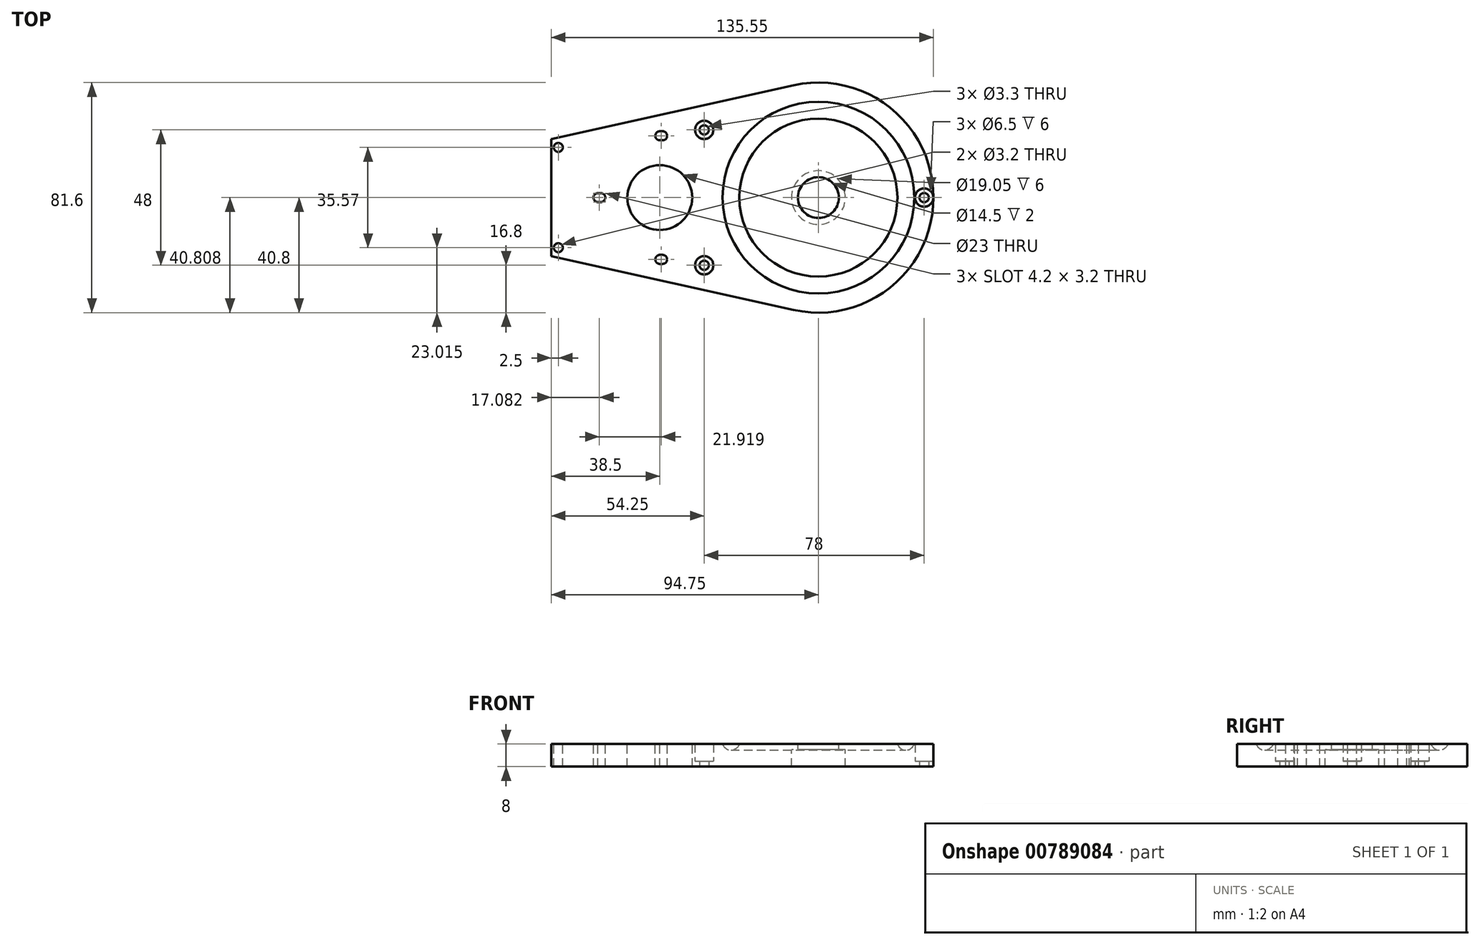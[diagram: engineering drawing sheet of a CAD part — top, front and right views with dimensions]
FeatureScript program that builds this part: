
annotation { "Feature Type Name" : "Feature", "Feature Type Description" : "" }
export const myFeature = defineFeature(function(context is Context, id is Id, definition is map)
    precondition{}
    {
        {
            var Q0;
            Q0=qCreatedBy(makeId("Top.planeOp"),FACE);
            var sketch = newSketch(context, id + "F0", { "sketchPlane" : qUnion([Q0])});
            skCircle(sketch, "E0", {"center": v(0, 0) * mm, "radius": 40.8 * mm});
            skSolve(sketch);
        }
        {
            var Q0;
            Q0=qSketchRegion(id+"F0",true);
            extrude(context, id + "F1", {"entities" : qUnion([Q0]), "depth" : 8 * mm, "offsetDistance" : 25 * mm});
        }
        {
            var Q0;
            Q0=qCreatedBy(makeId("Right.planeOp"),FACE);
            var sketch = newSketch(context, id + "F2", { "sketchPlane" : qUnion([Q0])});
            skLineSegment(sketch, "E1", {"start": v(0, 0) * mm, "end": v(0, 8) * mm});
            skLineSegment(sketch, "E2", {"start": v(0, 8) * mm, "end": v(7.25, 8) * mm});
            skLineSegment(sketch, "E3", {"start": v(7.25, 8) * mm, "end": v(7.25, 6) * mm});
            skLineSegment(sketch, "E4", {"start": v(7.25, 6) * mm, "end": v(9.53, 6) * mm});
            skLineSegment(sketch, "E5", {"start": v(9.53, 6) * mm, "end": v(9.53, 0) * mm});
            skLineSegment(sketch, "E6", {"start": v(9.53, 0) * mm, "end": v(0, 0) * mm});
            skLineSegment(sketch, "E7", {"start": v(0, 8) * mm, "end": v(0, 13.47) * mm, "construction": true});
            skSolve(sketch);
        }
        {
            var Q0;
            Q0=qSketchRegion(id+"F2",true);
            var Q1;
            Q1=sQuery(id+"F2.wireOp",EDGE,"E7");
            revolve(context, id + "F3", {"operationType" : NewBodyOperationType.REMOVE, "entities" : qUnion([Q0]), "axis" : qUnion([Q1]), "revolveType" : RevolveType.FULL, "oppositeDirection" : true});
        }
        {
            var Q0;
            Q0=qCreatedBy(makeId("Right.planeOp"),FACE);
            var sketch = newSketch(context, id + "F4", { "sketchPlane" : qUnion([Q0])});
            skCircle(sketch, "E8", {"center": v(31, 9) * mm, "radius": 3.15 * mm});
            skLineSegment(sketch, "E9", {"start": v(0, -0.8) * mm, "end": v(0, 13.57) * mm, "construction": true});
            skSolve(sketch);
        }
        {
            var Q0;
            Q0=qSketchRegion(id+"F4",true);
            var Q1;
            Q1=sQuery(id+"F4.wireOp",EDGE,"E9");
            revolve(context, id + "F5", {"operationType" : NewBodyOperationType.REMOVE, "entities" : qUnion([Q0]), "axis" : qUnion([Q1]), "revolveType" : RevolveType.FULL, "oppositeDirection" : true});
        }
        {
            var Q0;
            Q0=qCreatedBy(makeId("Top.planeOp"),FACE);
            var sketch = newSketch(context, id + "F6", { "sketchPlane" : qUnion([Q0])});
            skLineSegment(sketch, "E10.bottom", {"start": v(-36, 19.2) * mm, "end": v(-40.8, 19.2) * mm});
            skLineSegment(sketch, "E10.top", {"start": v(-36, -19.2) * mm, "end": v(-40.8, -19.2) * mm});
            skLineSegment(sketch, "E10.left", {"start": v(-36, 19.2) * mm, "end": v(-36, -19.2) * mm});
            skLineSegment(sketch, "E10.right", {"start": v(-40.8, 19.2) * mm, "end": v(-40.8, -19.2) * mm});
            skSolve(sketch);
        }
        {
            var Q0;
            Q0=qSketchRegion(id+"F6",true);
            extrude(context, id + "F7", {"entities" : qUnion([Q0]), "operationType" : NewBodyOperationType.REMOVE, "endBound" : BoundingType.THROUGH_ALL, "depth" : 25 * mm});
        }
        {
            var Q0;
            Q0=qCreatedBy(makeId("Top.planeOp"),FACE);
            var sketch = newSketch(context, id + "F8", { "sketchPlane" : qUnion([Q0])});
            skLineSegment(sketch, "E11", {"start": v(-94.75, -20.79) * mm, "end": v(-94.75, 20.79) * mm});
            skLineSegment(sketch, "E12", {"start": v(-94.75, 20.79) * mm, "end": v(-8.83, 39.83) * mm});
            skLineSegment(sketch, "E13", {"start": v(0, 0) * mm, "end": v(-51.86, 0) * mm, "construction": true});
            skArc(sketch, "E14.0", {"start": v(-8.83, 39.83) * mm, "mid": v(-24.68, 32.5) * mm, "end": v(-36, 19.2) * mm});
            skPoint(sketch, "E15.orphan", {"position": v(-36, -19.2) * mm});
            skLineSegment(sketch, "E16.MirrorCS", {"start": v(-94.75, -20.79) * mm, "end": v(-8.83, -39.83) * mm});
            skArc(sketch, "E17.MirrorCS", {"start": v(-8.83, -39.83) * mm, "mid": v(-24.68, -32.5) * mm, "end": v(-36, -19.2) * mm});
            skLineSegment(sketch, "E18", {"start": v(-36, 19.2) * mm, "end": v(-36, -19.2) * mm});
            skSolve(sketch);
        }
        {
            var Q0;
            Q0=qSketchRegion(id+"F8",true);
            var Q1;
            {var subQ0=sQuery(id+"F0.wireOp",EDGE,"E0");Q1=makeQuery(id+"F5.boolean.opBoolean","SPLIT",FACE,{"disambiguationData":[TD([makeQuery(id+"F1.opExtrude","SWEPT_FACE",FACE,{"disambiguationData":[OSD([subQ0])]})])],"derivedFrom":makeQuery(id+"F1.opExtrude","CAP_FACE",FACE,{"disambiguationData":[OSD([subQ0])],"isStart":false})});}
            extrude(context, id + "F9", {"entities" : qUnion([Q0]), "operationType" : NewBodyOperationType.ADD, "endBound" : BoundingType.UP_TO_SURFACE, "endBoundEntityFace" : qUnion([Q1]), "depth" : 25 * mm});
        }
        {
            var Q0;
            {var subQ0=sQuery(id+"F0.wireOp",EDGE,"E0");Q0=makeQuery(id+"F9.boolean.opBoolean","MERGE",FACE,{"derivedFrom":[makeQuery(id+"F5.boolean.opBoolean","SPLIT",FACE,{"disambiguationData":[TD([makeQuery(id+"F1.opExtrude","SWEPT_FACE",FACE,{"disambiguationData":[OSD([subQ0])]})])],"derivedFrom":makeQuery(id+"F1.opExtrude","CAP_FACE",FACE,{"disambiguationData":[OSD([subQ0])],"isStart":false})}),makeQuery(id+"F9.opExtrude","CAP_FACE",FACE,{"disambiguationData":[OSD([sQuery(id+"F8.wireOp",EDGE,"E11"),sQuery(id+"F8.wireOp",EDGE,"E12"),sQuery(id+"F8.wireOp",EDGE,"E14.0"),sQuery(id+"F8.wireOp",EDGE,"E16.MirrorCS"),sQuery(id+"F8.wireOp",EDGE,"E17.MirrorCS"),sQuery(id+"F8.wireOp",EDGE,"E18")])],"isStart":false})]});}
            var sketch = newSketch(context, id + "F10", { "sketchPlane" : qUnion([Q0])});
            skCircle(sketch, "E19", {"center": v(-56.25, 0) * mm, "radius": 11.5 * mm});
            skLineSegment(sketch, "E20", {"start": v(-56.25, 0) * mm, "end": v(0, 0) * mm, "construction": true});
            skLineSegment(sketch, "E21", {"start": v(-56.25, 0) * mm, "end": v(-94.75, 0) * mm, "construction": true});
            skLineSegment(sketch, "E22", {"start": v(-56.25, 0) * mm, "end": v(-99.42, 0) * mm, "construction": true});
            skCircle(sketch, "E23.3.0", {"center": v(-92.25, 17.79) * mm, "radius": 1.6 * mm});
            skCircle(sketch, "E24.MirrorC", {"center": v(-92.25, -17.79) * mm, "radius": 1.6 * mm});
            skLineSegment(sketch, "E25.bottom", {"start": v(-40.75, 15.5) * mm, "end": v(-71.75, 15.5) * mm, "construction": true});
            skLineSegment(sketch, "E25.top", {"start": v(-40.75, -15.5) * mm, "end": v(-71.75, -15.5) * mm, "construction": true});
            skLineSegment(sketch, "E25.left", {"start": v(-40.75, 15.5) * mm, "end": v(-40.75, -15.5) * mm, "construction": true});
            skLineSegment(sketch, "E25.right", {"start": v(-71.75, 15.5) * mm, "end": v(-71.75, -15.5) * mm, "construction": true});
            skCircle(sketch, "E26", {"center": v(-56.25, 0) * mm, "radius": 21.92 * mm, "construction": true});
            skLineSegment(sketch, "E27", {"start": v(-56.25, 23.52) * mm, "end": v(-55.25, 23.52) * mm});
            skLineSegment(sketch, "E28", {"start": v(-56.23, 20.32) * mm, "end": v(-55.25, 20.32) * mm});
            skArc(sketch, "E29", {"start": v(-55.25, 23.52) * mm, "mid": v(-53.65, 21.92) * mm, "end": v(-55.25, 20.32) * mm});
            skArc(sketch, "E30", {"start": v(-56.25, 23.52) * mm, "mid": v(-57.85, 21.91) * mm, "end": v(-56.23, 20.32) * mm});
            skLineSegment(sketch, "E31", {"start": v(-78.17, 1.6) * mm, "end": v(-77.17, 1.6) * mm});
            skLineSegment(sketch, "E32", {"start": v(-78.19, -1.6) * mm, "end": v(-77.17, -1.6) * mm});
            skArc(sketch, "E33", {"start": v(-77.17, 1.6) * mm, "mid": v(-75.57, 0) * mm, "end": v(-77.17, -1.6) * mm});
            skArc(sketch, "E34", {"start": v(-78.17, 1.6) * mm, "mid": v(-79.77, 0.02) * mm, "end": v(-78.19, -1.6) * mm});
            skLineSegment(sketch, "E35", {"start": v(-56.25, -20.32) * mm, "end": v(-55.25, -20.32) * mm});
            skLineSegment(sketch, "E36", {"start": v(-56.23, -23.52) * mm, "end": v(-55.25, -23.52) * mm});
            skArc(sketch, "E37", {"start": v(-55.25, -20.32) * mm, "mid": v(-53.65, -21.92) * mm, "end": v(-55.25, -23.52) * mm});
            skArc(sketch, "E38", {"start": v(-56.25, -20.32) * mm, "mid": v(-57.85, -21.93) * mm, "end": v(-56.23, -23.52) * mm});
            skSolve(sketch);
        }
        {
            var Q0;
            Q0=qSketchRegion(id+"F10",true);
            var Q1;
            Q1=makeQuery(id+"F10.imprint","IMPRINT",FACE,{"disambiguationData":[TD([[makeQuery(id+"F10.imprint","IMPRINT",EDGE,{"derivedFrom":sQuery(id+"F10.wireOp",EDGE,"4557ffc1-5d2f-461c-b845-0e4690cd48f1.3.0")}),1.0]])]});
            var Q2;
            Q2=makeQuery(id+"F10.imprint","IMPRINT",FACE,{"disambiguationData":[TD([[makeQuery(id+"F10.imprint","IMPRINT",EDGE,{"derivedFrom":sQuery(id+"F10.wireOp",EDGE,"HB3z2w4v-g97w-Ay5m-IKCo-CXgbghHc3kDH")}),1.0]])]});
            var Q3;
            Q3=makeQuery(id+"F10.imprint","IMPRINT",FACE,{"disambiguationData":[TD([[makeQuery(id+"F10.imprint","IMPRINT",EDGE,{"derivedFrom":sQuery(id+"F10.wireOp",EDGE,"4557ffc1-5d2f-461c-b845-0e4690cd48f1.1.0")}),1.0]])]});
            extrude(context, id + "F11", {"entities" : qUnion([Q0, Q1, Q2, Q3]), "operationType" : NewBodyOperationType.REMOVE, "endBound" : BoundingType.THROUGH_ALL, "oppositeDirection" : true, "offsetDistance" : 25 * mm, "depth" : 25 * mm});
        }
        {
            var Q0;
            {var subQ0=sQuery(id+"F0.wireOp",EDGE,"E0");Q0=makeQuery(id+"F9.boolean.opBoolean","MERGE",FACE,{"derivedFrom":[makeQuery(id+"F5.boolean.opBoolean","SPLIT",FACE,{"disambiguationData":[TD([makeQuery(id+"F1.opExtrude","SWEPT_FACE",FACE,{"disambiguationData":[OSD([subQ0])]})])],"derivedFrom":makeQuery(id+"F1.opExtrude","CAP_FACE",FACE,{"disambiguationData":[OSD([subQ0])],"isStart":false})}),makeQuery(id+"F9.opExtrude","CAP_FACE",FACE,{"disambiguationData":[OSD([sQuery(id+"F8.wireOp",EDGE,"E11"),sQuery(id+"F8.wireOp",EDGE,"E12"),sQuery(id+"F8.wireOp",EDGE,"E14.0"),sQuery(id+"F8.wireOp",EDGE,"E16.MirrorCS"),sQuery(id+"F8.wireOp",EDGE,"E17.MirrorCS"),sQuery(id+"F8.wireOp",EDGE,"E18")])],"isStart":false})]});}
            var sketch = newSketch(context, id + "F12", { "sketchPlane" : qUnion([Q0])});
            skPoint(sketch, "E39", {"position": v(-40.5, 24) * mm});
            skPoint(sketch, "E40", {"position": v(37.5, 0) * mm});
            skLineSegment(sketch, "E41", {"start": v(0, 0) * mm, "end": v(47.97, 0) * mm, "construction": true});
            skPoint(sketch, "E42.MirrorP", {"position": v(-40.5, -24) * mm});
            skSolve(sketch);
        }
        {
            var Q0;
            Q0=sQuery(id+"F12.wireOp",VERTEX,"E39");
            var Q1;
            Q1=sQuery(id+"F12.wireOp",VERTEX,"E42.MirrorP");
            var Q2;
            Q2=sQuery(id+"F12.wireOp",VERTEX,"E40");
            var Q3;
            Q3=makeQuery(id+"F1.opExtrude","SWEPT_BODY",BODY,{"disambiguationData":[OSD([sQuery(id+"F0.wireOp",EDGE,"E0")])]});
            hole(context, id + "F13", {"style" : HoleStyle.C_BORE, "endStyle" : HoleEndStyle.THROUGH, "holeDiameter" : 3.3 * mm, "cBoreDiameter" : 6.5 * mm, "cBoreDepth" : 6 * mm, "tappedDepth" : 12 * mm, "tapClearance" : 3, "locations" : qUnion([Q0, Q1, Q2]), "scope" : qUnion([Q3]), "majorDiameter" : 5 * mm, "startStyle" : HoleStartStyle.PART});
        }
    });
